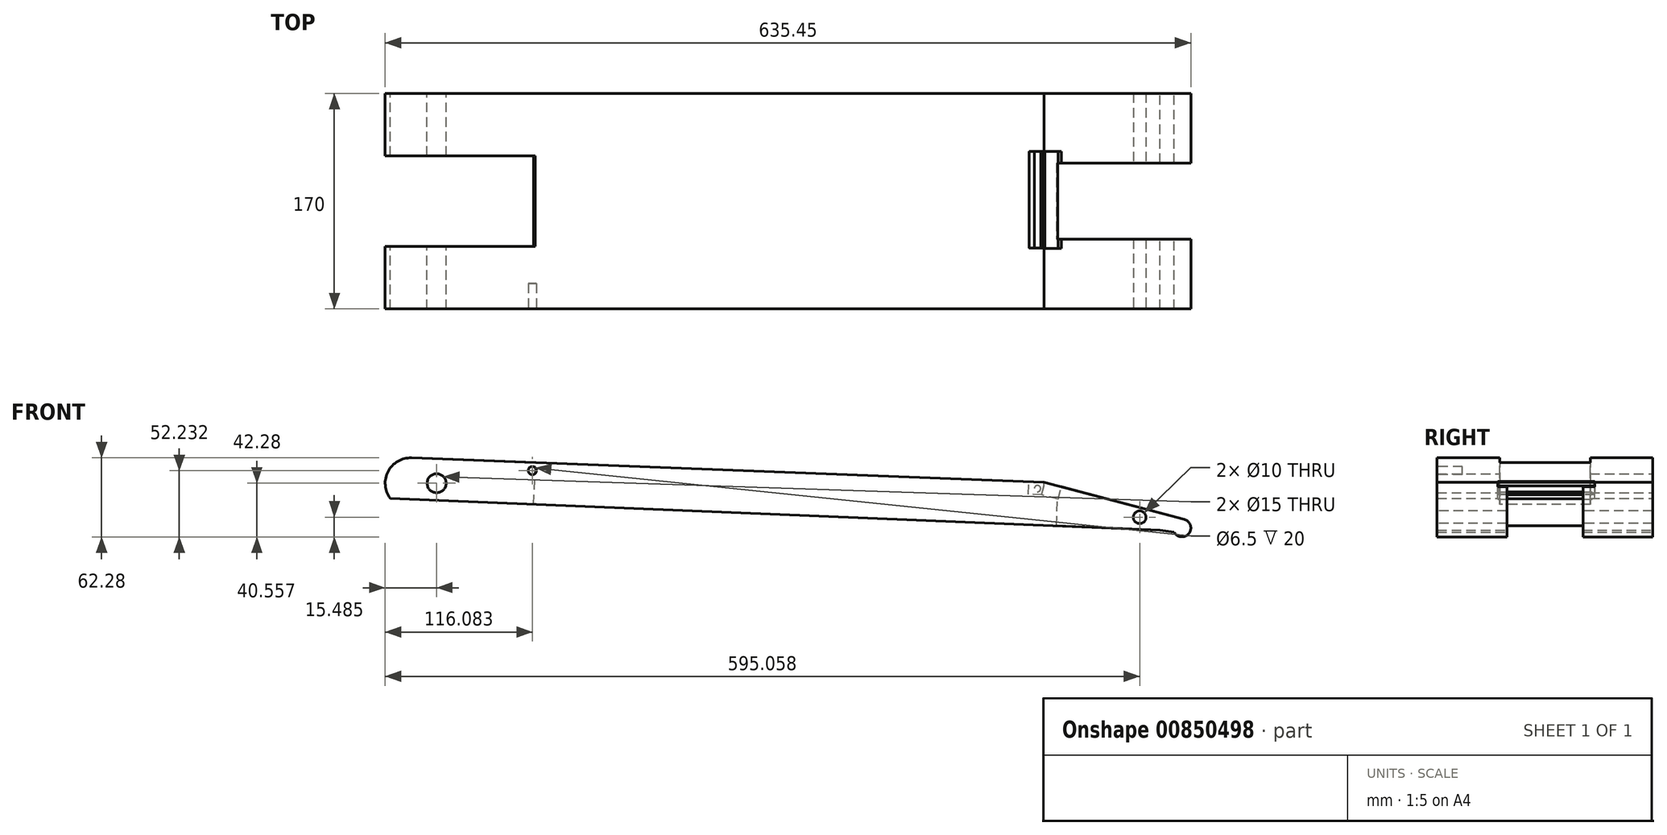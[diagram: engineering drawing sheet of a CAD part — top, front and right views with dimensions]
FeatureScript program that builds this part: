
annotation { "Feature Type Name" : "Feature", "Feature Type Description" : "" }
export const myFeature = defineFeature(function(context is Context, id is Id, definition is map)
    precondition{}
    {
        {
            var Q0;
            Q0=qCreatedBy(makeId("Front.planeOp"),FACE);
            var sketch = newSketch(context, id + "F0", { "sketchPlane" : qUnion([Q0])});
            skLineSegment(sketch, "E0", {"start": v(-220.24, 20.01) * mm, "end": v(279.4, 0.77) * mm});
            skArc(sketch, "E1", {"start": v(-219.47, 19.99) * mm, "mid": v(-240.23, 0.4) * mm, "end": v(-220.28, -20) * mm});
            skFitSpline(sketch, "E2", {"points": [v(-221.2, -19.98) * mm, v(-181.88, -21.5) * mm, v(-526.72, 0) * mm], "startDerivative": vector(79.3, -1.71) * mm, "endDerivative": vector(67.84, 31.02) * mm});
            skLineSegment(sketch, "E3", {"start": v(279.4, 0.77) * mm, "end": v(390.48, -28.64) * mm});
            skPoint(sketch, "E4.orphan", {"position": v(299.48, 0) * mm});
            skArc(sketch, "E5", {"start": v(382.06, -38.62) * mm, "mid": v(393.71, -39.6) * mm, "end": v(390, -28.51) * mm});
            skLineSegment(sketch, "E6", {"start": v(-526.72, 0) * mm, "end": v(373.67, -37) * mm});
            skLineSegment(sketch, "E7", {"start": v(370.86, -36.89) * mm, "end": v(382.06, -38.62) * mm});
            skSolve(sketch);
        }
        {
            var Q0;
            {var subQ3=sQuery(id+"F0.wireOp",EDGE,"nqfSfKfY-M8fa-TuKr-ETRJ-EszcfBgpJm2U");Q0=makeQuery(id+"F0.imprint","IMPRINT",FACE,{"disambiguationData":[TD([[makeQuery(id+"F0.imprint","IMPRINT",EDGE,{"derivedFrom":subQ3}),1.0]])]});}
            var Q1;
            Q1=makeQuery(id+"F0.imprint","IMPRINT",FACE,{"disambiguationData":[TD([[makeQuery(id+"F0.imprint","IMPRINT",EDGE,{"derivedFrom":sQuery(id+"F0.wireOp",EDGE,"BOHu1Tyl-tfMj-QQPF-xXF8-chUVmzv7brhG")}),1.0]])]});
            var Q2;
            {var subQ10=sQuery(id+"F0.wireOp",EDGE,"E5");Q2=makeQuery(id+"F0.imprint","IMPRINT",FACE,{"disambiguationData":[TD([[makeQuery(id+"F0.imprint","IMPRINT",EDGE,{"derivedFrom":subQ10}),1.0]])]});}
            extrude(context, id + "F1", {"entities" : qUnion([Q0, Q1, Q2]), "depth" : 170 * mm, "offsetDistance" : 25 * mm, "symmetric" : true});
        }
        {
            var Q0;
            Q0=makeQuery(id+"F1.opExtrude","SWEPT_FACE",FACE,{"disambiguationData":[OSD([sQuery(id+"F0.wireOp",EDGE,"E0")])]});
            var sketch = newSketch(context, id + "F2", { "sketchPlane" : qUnion([Q0])});
            skLineSegment(sketch, "E8.bottom", {"start": v(-262.5, 35.75) * mm, "end": v(-122.34, 35.75) * mm});
            skLineSegment(sketch, "E8.top", {"start": v(-262.5, -35.75) * mm, "end": v(-122.34, -35.75) * mm});
            skLineSegment(sketch, "E8.left", {"start": v(-262.5, 35.75) * mm, "end": v(-262.5, -35.75) * mm});
            skLineSegment(sketch, "E8.right", {"start": v(-122.34, 35.75) * mm, "end": v(-122.34, -35.75) * mm});
            skLineSegment(sketch, "E9.bottom", {"start": v(290.34, 30) * mm, "end": v(456.38, 30) * mm});
            skLineSegment(sketch, "E9.top", {"start": v(290.34, -30) * mm, "end": v(456.38, -30) * mm});
            skLineSegment(sketch, "E9.left", {"start": v(290.34, 30) * mm, "end": v(290.34, -30) * mm});
            skLineSegment(sketch, "E9.right", {"start": v(456.38, 30) * mm, "end": v(456.38, -30) * mm});
            skSolve(sketch);
        }
        {
            var Q0;
            Q0 = qSketchRegion(id + "F2", true);
            extrude(context, id + "F3", {"entities" : qUnion([Q0]), "operationType" : NewBodyOperationType.REMOVE, "oppositeDirection" : true, "depth" : 60 * mm, "offsetDistance" : 25 * mm});
        }
        {
            var Q0;
            Q0=makeQuery(id+"F3.boolean.opBoolean","COPY",FACE,{"derivedFrom":makeQuery(id+"F3.opExtrude","SWEPT_FACE",FACE,{"disambiguationData":[OSD([sQuery(id+"F2.wireOp",EDGE,"E9.top")])]})});
            var sketch = newSketch(context, id + "F4", { "sketchPlane" : qUnion([Q0])});
            skCircle(sketch, "E10", {"center": v(-354.82, -26.8) * mm, "radius": 5 * mm});
            skSolve(sketch);
        }
        {
            var Q0;
            Q0 = qSketchRegion(id + "F4", true);
            extrude(context, id + "F5", {"entities" : qUnion([Q0]), "operationType" : NewBodyOperationType.REMOVE, "endBound" : BoundingType.THROUGH_ALL, "depth" : 25 * mm, "offsetDistance" : 25 * mm, "hasSecondDirection" : true, "secondDirectionBound" : BoundingType.THROUGH_ALL, "secondDirectionOppositeDirection" : true, "secondDirectionDepth" : 25 * mm});
        }
        {
            var Q0;
            Q0=makeQuery(id+"F3.boolean.opBoolean","COPY",FACE,{"derivedFrom":makeQuery(id+"F3.opExtrude","SWEPT_FACE",FACE,{"disambiguationData":[OSD([sQuery(id+"F2.wireOp",EDGE,"E8.bottom")])]})});
            var sketch = newSketch(context, id + "F6", { "sketchPlane" : qUnion([Q0])});
            skCircle(sketch, "E11", {"center": v(-199.68, 0) * mm, "radius": 7.5 * mm});
            skSolve(sketch);
        }
        {
            var Q0;
            Q0=makeQuery(id+"F6.imprint","IMPRINT",FACE,{"disambiguationData":[TD([[makeQuery(id+"F6.imprint","IMPRINT",EDGE,{"derivedFrom":sQuery(id+"F6.wireOp",EDGE,"E11")}),1.0]])]});
            var Q1;
            Q1 = qSketchRegion(id + "F8", true);
            extrude(context, id + "F7", {"entities" : qUnion([Q0, Q1]), "operationType" : NewBodyOperationType.REMOVE, "endBound" : BoundingType.THROUGH_ALL, "depth" : 25 * mm, "offsetDistance" : 25 * mm, "hasSecondDirection" : true, "secondDirectionBound" : BoundingType.THROUGH_ALL, "secondDirectionOppositeDirection" : true, "secondDirectionDepth" : 25 * mm});
        }
        {
            var Q0;
            Q0=makeQuery(id+"F1.opExtrude","SWEPT_FACE",FACE,{"disambiguationData":[OSD([sQuery(id+"F0.wireOp",EDGE,"E3")])]});
            var sketch = newSketch(context, id + "F8", { "sketchPlane" : qUnion([Q0])});
            skLineSegment(sketch, "E12.bottom", {"start": v(284.16, -37.16) * mm, "end": v(270.5, -37.16) * mm});
            skLineSegment(sketch, "E12.top", {"start": v(284.16, 39.3) * mm, "end": v(270.5, 39.3) * mm});
            skLineSegment(sketch, "E12.left", {"start": v(284.16, -37.16) * mm, "end": v(284.16, 39.3) * mm});
            skLineSegment(sketch, "E12.right", {"start": v(270.5, -37.16) * mm, "end": v(270.5, 39.3) * mm});
            skSolve(sketch);
        }
        {
            var Q0;
            Q0=makeQuery(id+"F8.imprint","IMPRINT",FACE,{"disambiguationData":[TD([[makeQuery(id+"F8.imprint","IMPRINT",EDGE,{"derivedFrom":sQuery(id+"F8.wireOp",EDGE,"E12.bottom")}),-1.0]])]});
            extrude(context, id + "F9", {"entities" : qUnion([Q0]), "operationType" : NewBodyOperationType.REMOVE, "oppositeDirection" : true, "depth" : 10 * mm, "offsetDistance" : 25 * mm});
        }
        {
            var Q0;
            Q0=makeQuery(id+"F9.boolean.opBoolean","COPY",FACE,{"derivedFrom":makeQuery(id+"F9.opExtrude","SWEPT_FACE",FACE,{"disambiguationData":[OSD([sQuery(id+"F0.wireOp",EDGE,"E3"),sQuery(id+"F2.wireOp",EDGE,"E9.top")])]})});
            extrude(context, id + "F10", {"entities" : qUnion([Q0]), "operationType" : NewBodyOperationType.REMOVE, "oppositeDirection" : true, "depth" : 60 * mm, "offsetDistance" : 25 * mm});
        }
        {
            var Q0;
            Q0=makeQuery(id+"F1.opExtrude","SWEPT_FACE",FACE,{"disambiguationData":[OSD([sQuery(id+"F0.wireOp",EDGE,"E0")])]});
            var sketch = newSketch(context, id + "F11", { "sketchPlane" : qUnion([Q0])});
            skLineSegment(sketch, "E13.bottom", {"start": v(279.15, 39.24) * mm, "end": v(267.3, 39.24) * mm});
            skLineSegment(sketch, "E13.top", {"start": v(279.15, -37.1) * mm, "end": v(267.3, -37.1) * mm});
            skLineSegment(sketch, "E13.left", {"start": v(279.15, 39.24) * mm, "end": v(279.15, -37.1) * mm});
            skLineSegment(sketch, "E13.right", {"start": v(267.3, 39.24) * mm, "end": v(267.3, -37.1) * mm});
            skSolve(sketch);
        }
        {
            var Q0;
            Q0 = qSketchRegion(id + "F11", true);
            extrude(context, id + "F12", {"entities" : qUnion([Q0]), "operationType" : NewBodyOperationType.REMOVE, "oppositeDirection" : true, "depth" : 10 * mm, "offsetDistance" : 25 * mm});
        }
        {
            var Q0;
            Q0=makeQuery(id+"F12.boolean.opBoolean","COPY",FACE,{"derivedFrom":makeQuery(id+"F12.opExtrude","SWEPT_FACE",FACE,{"disambiguationData":[OSD([sQuery(id+"F11.wireOp",EDGE,"E13.bottom")])]})});
            var sketch = newSketch(context, id + "F13", { "sketchPlane" : qUnion([Q0])});
            skCircle(sketch, "E14", {"center": v(274.22, -4.3) * mm, "radius": 2.5 * mm});
            skSolve(sketch);
        }
        {
            var Q0;
            Q0=makeQuery(id+"F13.imprint","IMPRINT",FACE,{"disambiguationData":[TD([[makeQuery(id+"F13.imprint","IMPRINT",EDGE,{"derivedFrom":sQuery(id+"F13.wireOp",EDGE,"E14")}),1.0]])]});
            extrude(context, id + "F14", {"entities" : qUnion([Q0]), "operationType" : NewBodyOperationType.ADD, "endBound" : BoundingType.UP_TO_NEXT, "depth" : 25 * mm, "offsetDistance" : 25 * mm});
        }
        {
            var Q0;
            Q0=makeQuery(id+"F1.opExtrude","CAP_FACE",FACE,{"disambiguationData":[OSD([sQuery(id+"F0.wireOp",EDGE,"E0"),sQuery(id+"F0.wireOp",EDGE,"E1"),sQuery(id+"F0.wireOp",EDGE,"E2"),sQuery(id+"F0.wireOp",EDGE,"E3"),sQuery(id+"F0.wireOp",EDGE,"E5"),sQuery(id+"F0.wireOp",EDGE,"E6"),sQuery(id+"F0.wireOp",EDGE,"E7")])],"isStart":false});
            var sketch = newSketch(context, id + "F15", { "sketchPlane" : qUnion([Q0])});
            skCircle(sketch, "E15", {"center": v(-124.16, 9.95) * mm, "radius": 3.25 * mm});
            skSolve(sketch);
        }
        {
            var Q0;
            Q0=makeQuery(id+"F15.imprint","IMPRINT",FACE,{"disambiguationData":[TD([[makeQuery(id+"F15.imprint","IMPRINT",EDGE,{"derivedFrom":sQuery(id+"F15.wireOp",EDGE,"E15")}),1.0]])]});
            extrude(context, id + "F16", {"entities" : qUnion([Q0]), "operationType" : NewBodyOperationType.REMOVE, "oppositeDirection" : true, "depth" : 20 * mm, "offsetDistance" : 25 * mm});
        }
    });
